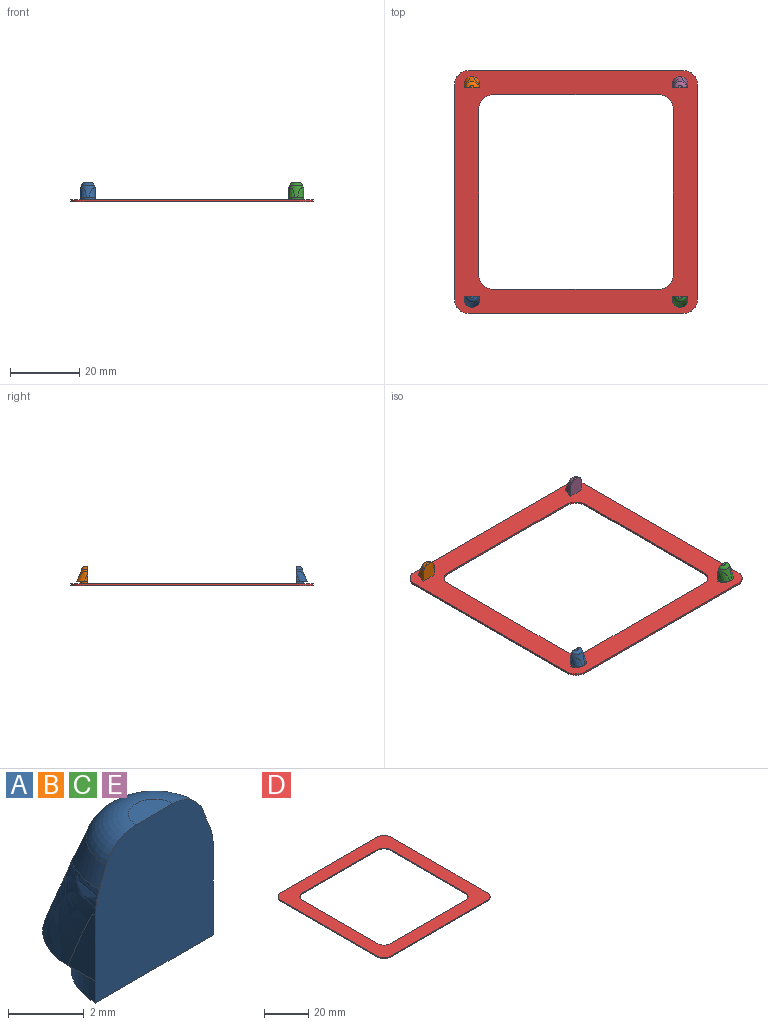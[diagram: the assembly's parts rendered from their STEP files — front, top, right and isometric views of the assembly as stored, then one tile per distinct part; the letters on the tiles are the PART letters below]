
ASSEMBLY  parts=5 mates=4
PART A: 11 faces, bbox 6.7x3.8x5.8 mm
  f0: cone r=1.8mm half-angle=21.6deg, axis (0,0,-1), area 9.7mm2, adj f1,f2,f6,f9,f10
  f1: plane 4.65x3.45mm, normal (0,0,-1), area 4.6mm2, adj f0,f3,f7,f8,f9,f10
  f2: plane 5x4.4mm, normal (0,-1,0), area 20.5mm2, adj f0,f3,f4,f5,f6,f7,f8,f9
  f3: cylinder r=2.2mm len=4.4mm, axis (0,0,1), area 4.8mm2, adj f1,f2,f4
  f4: plane 4.4x2.2mm, normal (0,0,-1), area 7.6mm2, adj f2,f3
  f5: plane 1.37x0.68mm, normal (0,0,1), area 0.7mm2, adj f2,f6
  f6: torus R=0.68mm, axis (0,0,1), area 5.9mm2, adj f0,f2,f5
  f7: plane 2.15x1.03mm, normal (1,0,0), area 1.2mm2, adj f1,f2,f10
  f8: plane 2.15x1.03mm, normal (-1,0,0), area 1.2mm2, adj f1,f2,f9
  f9: bspline ~4.14x3.56mm, area 7.5mm2, adj f0,f1,f2,f8
  f10: bspline ~4.14x3.56mm, area 7.5mm2, adj f0,f1,f2,f7
PART B: same geometry as A
PART C: same geometry as A
PART D: 18 faces, bbox 70x70x0.5 mm
  f0: cylinder r=4mm len=4mm, axis (0,0,1), area 3.1mm2, adj f1,f11,f12,f13
  f1: plane 62x0.5mm, normal (0,1,0), area 31mm2, adj f0,f2,f12,f13
  f2: cylinder r=4mm len=4mm, axis (0,0,1), area 3.1mm2, adj f1,f3,f12,f13
  f3: plane 62x0.5mm, normal (-1,0,0), area 31mm2, adj f2,f4,f12,f13
  f4: cylinder r=4mm len=4mm, axis (0,0,1), area 3.1mm2, adj f3,f5,f12,f13
  f5: plane 62x0.5mm, normal (0,-1,0), area 31mm2, adj f4,f6,f12,f13
  f6: cylinder r=4mm len=4mm, axis (0,0,1), area 3.1mm2, adj f5,f11,f12,f13
  f7: plane 48x0.5mm, normal (0,-1,0), area 24mm2, adj f12,f13,f14,f17
  f8: plane 48x0.5mm, normal (-1,0,0), area 24mm2, adj f12,f13,f14,f15
  f9: plane 48x0.5mm, normal (0,1,0), area 24mm2, adj f12,f13,f15,f16
  f10: plane 48x0.5mm, normal (1,0,0), area 24mm2, adj f12,f13,f16,f17
  f11: plane 62x0.5mm, normal (1,0,0), area 31mm2, adj f0,f6,f12,f13
  f12: plane 70x70mm, normal (0,0,-1), area 1764mm2, adj f0,f1,f2,f3,f4,f5,f6,f7
  f13: plane 70x70mm, normal (0,0,1), area 1764mm2, adj f0,f1,f2,f3,f4,f5,f6,f7
  f14: cylinder r=4mm len=4mm, axis (0,0,-1), area 3.1mm2, adj f7,f8,f12,f13
  f15: cylinder r=4mm len=4mm, axis (0,0,1), area 3.1mm2, adj f8,f9,f12,f13
  f16: cylinder r=4mm len=4mm, axis (0,0,-1), area 3.1mm2, adj f9,f10,f12,f13
  f17: cylinder r=4mm len=4mm, axis (0,0,1), area 3.1mm2, adj f7,f10,f12,f13
PART E: same geometry as A
PLACE A rot(axis=(0,0,1),180deg) t=(-19.9,-33.53,2.06)mm
PLACE B t=(-19.9,26.47,2.06)mm
PLACE C rot(axis=(0,0,1),180deg) t=(40.1,-33.53,2.06)mm
PLACE D t=(10.1,-3.53,2.06)mm
PLACE E t=(40.1,26.47,2.06)mm
MATE fastened A.f3 <-> D.f13  axis (0,0,-1) through (-19.9,-33.53,2.06)mm
MATE fastened E.f3 <-> D.f13  axis (0,0,-1) through (40.1,26.47,2.06)mm
MATE fastened B.f3 <-> D.f13  axis (0,0,-1) through (-19.9,26.47,2.06)mm
MATE fastened C.f3 <-> D.f13  axis (0,0,-1) through (40.1,-33.53,2.06)mm
